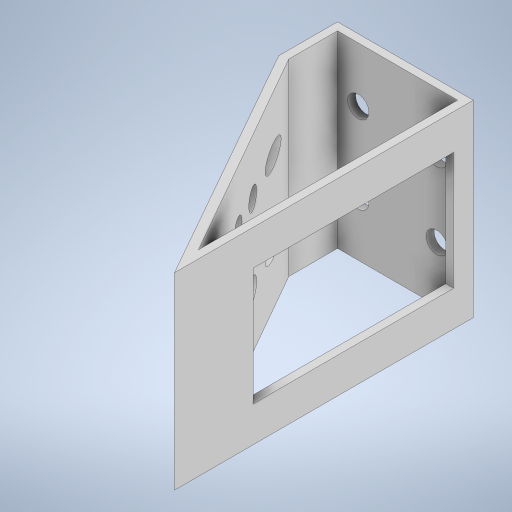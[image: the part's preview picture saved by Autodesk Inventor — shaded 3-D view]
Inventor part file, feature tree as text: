
AUTODESK INVENTOR PART (.ipt)
format: ipt  version: 2024.2 (Build 282272000, 272)  size: 363,008 bytes
history: native  units: in
note: dims shown in document units (in); Inventor stores cm internally (conversion verified against a paired STEP export)
features: extrude x7, sketch x5, thicken_offset x2, hole x1
ambient origin geometry x8: Origin, YZ Plane, XZ Plane, XY Plane, X Axis, Y Axis, Z Axis, Center Point
bodies: Solid1 (feature_tree)
feature tree (15):
  extrude  "Extrusion1"  Depth=1.73in
  extrude  "Extrusion5"  Depth=2.4in TaperAngle=0.0deg
  sketch  "Sketch2"  dims[d2=0.4157in d3=2.4in d4=0.0in]
  hole  "Hole1"  [1 undecoded]
  extrude  "Extrusion6"  Depth=0.9843in
  extrude  "Extrusion7"  Depth=0.5in
  sketch  "Sketch8"  dims[d9=0.5in d10=0.5in d11=0.5in d12=0.5in d13=0.2543in d14=0.551in d15=0.375in d16=0.25in d17=0.5635in d18=1.0in d19=0.8108in d26=0.1in d27=3.0in d28=0.0in d29=0.27in d30=0.27in d31=0.27in d32=0.27in d33=0.27in d34=0.27in d35=0.27in d36=0.27in d37=0.27in d38=0.2in d39=0.0in d40=0.25in d41=0.2in d42=0.0in d43=0.5in d44=0.5in d45=1.0in d47=1.0in d48=1.0in d49=0.27in d50=0.27in d51=0.27in d52=0.27in d53=0.2in d54=0.0in d69=4.0in d70=0.0in d71=1.0in d72=0.0in d75=0.2in d76=0.2in d77=0.2in d78=0.2in]
  extrude  "Extrusion8"  Depth=0.5in
  extrude  "Extrusion9"  Depth=0.5in
  extrude  "Extrusion10"  Depth=0.1in
  thicken_offset  "Thicken2"
  thicken_offset  "Thicken3"
  sketch  "Sketch1"  dims[d0=0.75in d1=1.73in]
  sketch  "Sketch6"  dims[d5=0.5565in d6=2.4in]
  sketch  "Sketch7"  dims[d7=1.2in d8=0.9843in]
note: 1 required parameter value undecoded (feature->parameter linkage not recoverable at this tier; creation-order binding heuristic only, values carry confidence <= 0.55)
